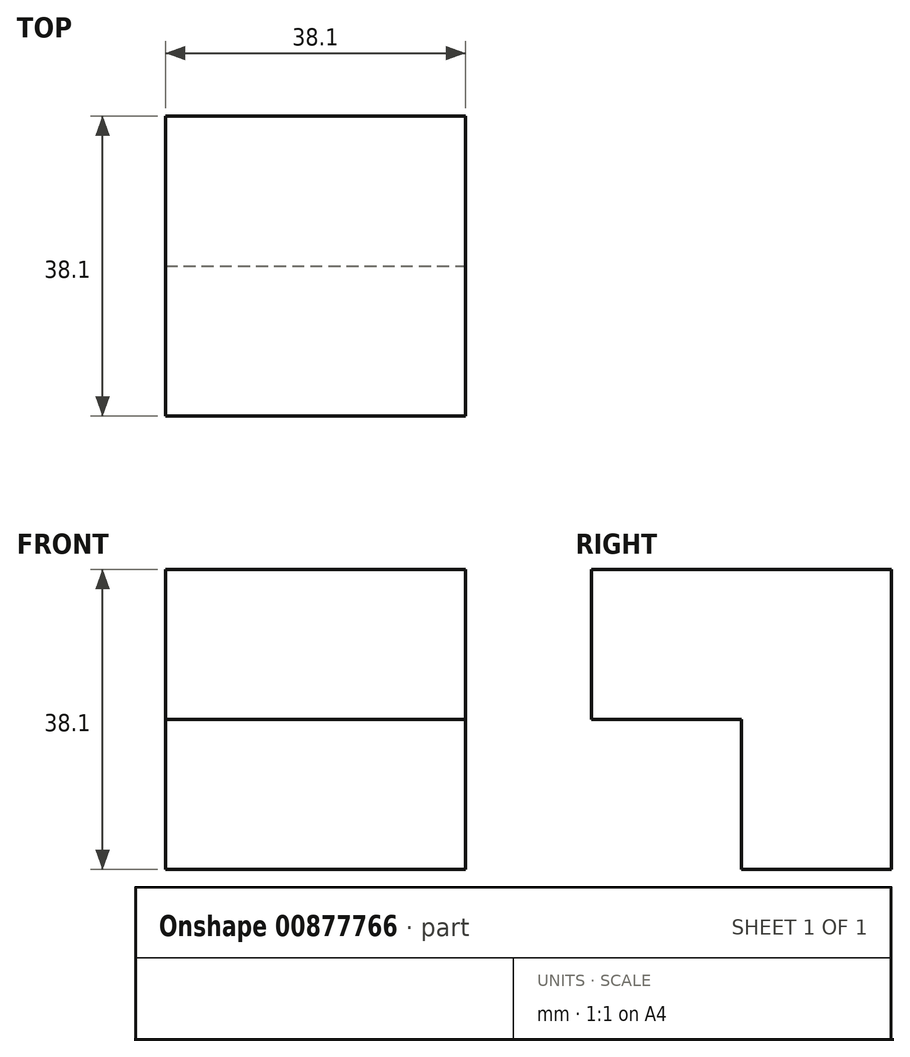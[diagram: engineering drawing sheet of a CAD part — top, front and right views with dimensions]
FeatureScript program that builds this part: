
annotation { "Feature Type Name" : "Feature", "Feature Type Description" : "" }
export const myFeature = defineFeature(function(context is Context, id is Id, definition is map)
    precondition{}
    {
        {
            var Q0;
            Q0=qCreatedBy(makeId("Right.planeOp"),FACE);
            var sketch = newSketch(context, id + "F0", { "sketchPlane" : qUnion([Q0])});
            skLineSegment(sketch, "E0.bottom", {"start": v(0, 0) * mm, "end": v(-19.05, 0) * mm});
            skLineSegment(sketch, "E0.top", {"start": v(0, 38.1) * mm, "end": v(-19.05, 38.1) * mm});
            skLineSegment(sketch, "E0.left", {"start": v(0, 0) * mm, "end": v(0, 38.1) * mm});
            skLineSegment(sketch, "E0.right", {"start": v(-19.05, 0) * mm, "end": v(-19.05, 38.1) * mm});
            skLineSegment(sketch, "E1.bottom", {"start": v(-19.05, 38.1) * mm, "end": v(-38.1, 38.1) * mm});
            skLineSegment(sketch, "E1.top", {"start": v(-19.05, 19.05) * mm, "end": v(-38.1, 19.05) * mm});
            skLineSegment(sketch, "E1.left", {"start": v(-19.05, 38.1) * mm, "end": v(-19.05, 19.05) * mm});
            skLineSegment(sketch, "E1.right", {"start": v(-38.1, 38.1) * mm, "end": v(-38.1, 19.05) * mm});
            skSolve(sketch);
        }
        {
            var Q0;
            Q0=qSketchRegion(id+"F0",true);
            extrude(context, id + "F1", {"entities" : qUnion([Q0]), "oppositeDirection" : true, "depth" : 19.05 * mm});
        }
        {
            var Q0;
            Q0=qCreatedBy(makeId("Right.planeOp"),FACE);
            var sketch = newSketch(context, id + "F2", { "sketchPlane" : qUnion([Q0])});
            skLineSegment(sketch, "E2.bottom", {"start": v(0, 38.1) * mm, "end": v(-38.1, 38.1) * mm});
            skLineSegment(sketch, "E2.top", {"start": v(0, 19.05) * mm, "end": v(-38.1, 19.05) * mm});
            skLineSegment(sketch, "E2.left", {"start": v(0, 38.1) * mm, "end": v(0, 19.05) * mm});
            skLineSegment(sketch, "E2.right", {"start": v(-38.1, 38.1) * mm, "end": v(-38.1, 19.05) * mm});
            skSolve(sketch);
        }
        {
            var Q0;
            Q0=qSketchRegion(id+"F2",true);
            extrude(context, id + "F3", {"entities" : qUnion([Q0]), "operationType" : NewBodyOperationType.ADD, "oppositeDirection" : true, "depth" : 38.1 * mm});
        }
        {
            var Q0;
            Q0=makeQuery(id+"F1.opExtrude","CAP_FACE",FACE,{"disambiguationData":[OSD([sQuery(id+"F0.wireOp",EDGE,"E0.bottom"),sQuery(id+"F0.wireOp",EDGE,"E0.top"),sQuery(id+"F0.wireOp",EDGE,"E0.left"),sQuery(id+"F0.wireOp",EDGE,"E0.right"),sQuery(id+"F0.wireOp",EDGE,"E1.bottom"),sQuery(id+"F0.wireOp",EDGE,"E1.top"),sQuery(id+"F0.wireOp",EDGE,"E1.right")])],"isStart":false});
            extrude(context, id + "F4", {"entities" : qUnion([Q0]), "operationType" : NewBodyOperationType.ADD, "depth" : 19.05 * mm});
        }
    });
